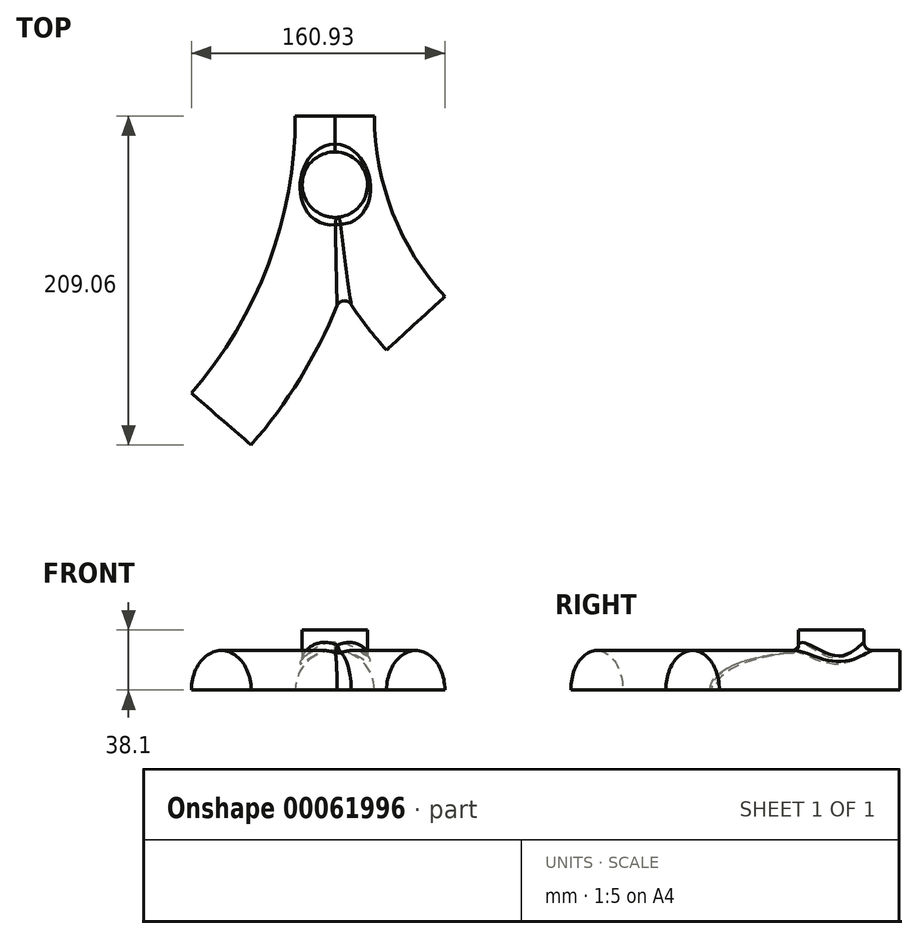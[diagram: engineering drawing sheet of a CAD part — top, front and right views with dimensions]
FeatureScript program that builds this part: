
annotation { "Feature Type Name" : "Feature", "Feature Type Description" : "" }
export const myFeature = defineFeature(function(context is Context, id is Id, definition is map)
    precondition{}
    {
        {
            var Q0;
            Q0=qCreatedBy(makeId("Top.planeOp"),FACE);
            var sketch = newSketch(context, id + "F0", { "sketchPlane" : qUnion([Q0])});
            skLineSegment(sketch, "E0", {"start": v(0, 0) * mm, "end": v(0, -43.68) * mm});
            skCircle(sketch, "E1", {"center": v(0, -43.68) * mm, "radius": 20.77 * mm});
            skSolve(sketch);
        }
        {
            var Q0;
            {var subQ0=sQuery(id+"F0.wireOp",EDGE,"E1");Q0=makeQuery(id+"F0.imprint","IMPRINT",FACE,{"disambiguationData":[TD([[makeQuery(id+"F0.imprint","IMPRINT",EDGE,{"derivedFrom":subQ0}),1.0]])]});}
            extrude(context, id + "F1", {"entities" : qUnion([Q0]), "depth" : 38.1 * mm});
        }
        {
            var Q0;
            Q0=qCreatedBy(makeId("Top.planeOp"),FACE);
            var sketch = newSketch(context, id + "F2", { "sketchPlane" : qUnion([Q0])});
            skArc(sketch, "E2", {"start": v(0, 0) * mm, "mid": v(13.3, -70.7) * mm, "end": v(51.35, -131.73) * mm});
            skArc(sketch, "E3", {"start": v(-72.14, -192.55) * mm, "mid": v(-18.63, -102.8) * mm, "end": v(0, 0) * mm});
            skLineSegment(sketch, "E4", {"start": v(0, 0) * mm, "end": v(0, -167.15) * mm, "construction": true});
            skSolve(sketch);
        }
        {
            var Q0;
            Q0=qCreatedBy(makeId("Front.planeOp"),FACE);
            var sketch = newSketch(context, id + "F3", { "sketchPlane" : qUnion([Q0])});
            skLineSegment(sketch, "E5", {"start": v(25.13, 0) * mm, "end": v(-25.13, 0) * mm});
            skArc(sketch, "E6", {"start": v(25.13, 0) * mm, "mid": v(0, 25.13) * mm, "end": v(-25.13, 0) * mm});
            skSolve(sketch);
        }
        {
            var Q0;
            Q0=makeQuery(id+"F3.imprint","IMPRINT",FACE,{"disambiguationData":[TD([[makeQuery(id+"F3.imprint","IMPRINT",EDGE,{"derivedFrom":sQuery(id+"F3.wireOp",EDGE,"E5")}),-1.0]])]});
            var Q1;
            Q1=sQuery(id+"F3.wireOp",EDGE,"E5");
            var Q2;
            Q2=sQuery(id+"F2.wireOp",EDGE,"E3");
            sweep(context, id + "F4", {"profiles" : qUnion([Q0]), "surfaceProfiles" : qUnion([Q1]), "path" : qUnion([Q2])});
        }
        {
            var Q0;
            Q0=makeQuery(id+"F3.imprint","IMPRINT",FACE,{"disambiguationData":[TD([[makeQuery(id+"F3.imprint","IMPRINT",EDGE,{"derivedFrom":sQuery(id+"F3.wireOp",EDGE,"E5")}),-1.0]])]});
            var Q1;
            Q1=sQuery(id+"F2.wireOp",EDGE,"E2");
            sweep(context, id + "F5", {"operationType" : NewBodyOperationType.ADD, "profiles" : qUnion([Q0]), "path" : qUnion([Q1])});
        }
        {
            var Q0;
            {var subQ0=sQuery(id+"F3.wireOp",EDGE,"E6");Q0=makeQuery(id+"F5.boolean.opBoolean","INTERSECT",EDGE,{"disambiguationData":[OD(1.0)],"derivedFrom":[makeQuery(id+"F4.opSweep","SWEPT_FACE",FACE,{"disambiguationData":[OSD([sQuery(id+"F2.wireOp",EDGE,"E3"),subQ0])]}),makeQuery(id+"F5.opSweep","SWEPT_FACE",FACE,{"disambiguationData":[OSD([sQuery(id+"F2.wireOp",EDGE,"E2"),subQ0])]})]});}
            var Q1;
            Q1=makeQuery(id+"F5.boolean.opBoolean","INTERSECT",EDGE,{"derivedFrom":[makeQuery(id+"F1.opExtrude","SWEPT_FACE",FACE,{"disambiguationData":[OSD([sQuery(id+"F0.wireOp",EDGE,"E1")])]}),makeQuery(id+"F4.opSweep","SWEPT_FACE",FACE,{"disambiguationData":[OSD([sQuery(id+"F2.wireOp",EDGE,"E3"),sQuery(id+"F3.wireOp",EDGE,"E6")])]})]});
            var Q2;
            Q2=makeQuery(id+"F5.boolean.opBoolean","INTERSECT",EDGE,{"derivedFrom":[makeQuery(id+"F1.opExtrude","SWEPT_FACE",FACE,{"disambiguationData":[OSD([sQuery(id+"F0.wireOp",EDGE,"E1")])]}),makeQuery(id+"F5.opSweep","SWEPT_FACE",FACE,{"disambiguationData":[OSD([sQuery(id+"F2.wireOp",EDGE,"E2"),sQuery(id+"F3.wireOp",EDGE,"E6")])]})]});
            fillet(context, id + "F6", {"entities" : qUnion([Q0, Q1, Q2]), "radius" : 5.08 * mm, "tangentPropagation" : true, "allowEdgeOverflow" : false});
        }
    });
